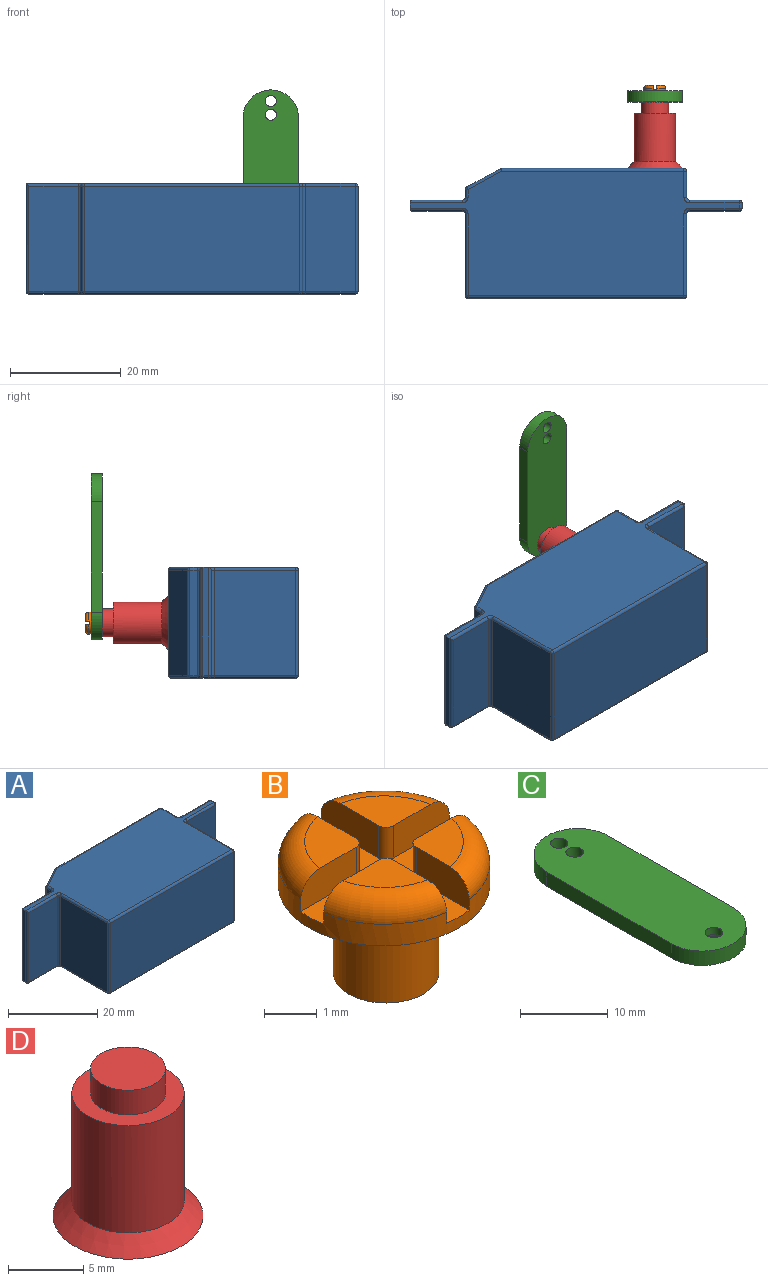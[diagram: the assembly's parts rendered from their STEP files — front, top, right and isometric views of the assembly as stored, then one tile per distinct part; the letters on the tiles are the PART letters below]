
ASSEMBLY  parts=4 mates=3
PART A: 77 faces, bbox 60x23.5x20 mm
  f0: plane 19x1.43mm, normal (-1,0,0), area 27.2mm2, adj f65,f70,f73,f76
  f1: plane 19x9mm, normal (0,1,0), area 171mm2, adj f64,f68,f72,f73
  f2: plane 19.5x1mm, normal (-1,0,0), area 19.5mm2, adj f13,f51,f59,f68
  f3: plane 19x9mm, normal (0,-1,0), area 171mm2, adj f42,f47,f51,f52
  f4: plane 19x14.77mm, normal (-1,0,0), area 280.6mm2, adj f32,f37,f42,f43
  f5: plane 39x19mm, normal (0,-1,0), area 741mm2, adj f22,f27,f32,f33
  f6: plane 19x14.77mm, normal (1,0,0), area 280.6mm2, adj f16,f17,f22,f23
  f7: plane 19x9mm, normal (0,-1,0), area 171mm2, adj f15,f16,f25,f26
  f8: plane 19x1mm, normal (1,0,0), area 19mm2, adj f24,f25,f35,f36
  f9: plane 19x9mm, normal (0,1,0), area 171mm2, adj f34,f35,f45,f46
  f10: plane 19x4.73mm, normal (1,0,0), area 89.9mm2, adj f44,f45,f54,f55
  f11: plane 32.89x19mm, normal (0,1,0), area 625mm2, adj f53,f54,f61,f62
  f12: plane 19x6.11mm, normal (-0.48,0.88,0), area 131.8mm2, adj f60,f61,f70,f71
  f13: plane 59.5x22.5mm, normal (0,0,1), area 888.8mm2, adj f2,f17,f20,f26,f27,f36,f37,f41
  f14: plane 59x22.5mm, normal (0,0,-1), area 888.3mm2, adj f15,f18,f23,f24,f33,f34,f39,f43
  f15: cylinder r=0.5mm len=9mm, axis (1,0,0), area 7.1mm2, adj f7,f14,f18,f19
  f16: cylinder r=0.5mm len=19mm, axis (0,0,-1), area 14.9mm2, adj f6,f7,f18,f20
  f17: cylinder r=0.5mm len=14.77mm, axis (0,-1,0), area 11.6mm2, adj f6,f13,f20,f21
  f18: torus R=1mm, axis (0,0,1), area 0.8mm2, adj f14,f15,f16,f23
  f19: sphere r=0.5mm, area 0.4mm2, adj f15,f24,f25
  f20: torus R=1mm, axis (0,0,1), area 0.8mm2, adj f13,f16,f17,f26
  f21: sphere r=0.5mm, area 0.4mm2, adj f17,f22,f27
  f22: cylinder r=0.5mm len=19mm, axis (0,0,1), area 14.9mm2, adj f5,f6,f21,f28
  f23: cylinder r=0.5mm len=14.77mm, axis (0,1,0), area 11.6mm2, adj f6,f14,f18,f28
  f24: cylinder r=0.5mm len=1mm, axis (0,1,0), area 0.8mm2, adj f8,f14,f19,f29
  f25: cylinder r=0.5mm len=19mm, axis (0,0,1), area 14.9mm2, adj f7,f8,f19,f30
  f26: cylinder r=0.5mm len=9mm, axis (-1,0,0), area 7.1mm2, adj f7,f13,f20,f30
  f27: cylinder r=0.5mm len=39mm, axis (-1,0,0), area 30.6mm2, adj f5,f13,f21,f31
  f28: sphere r=0.5mm, area 0.4mm2, adj f22,f23,f33
  f29: sphere r=0.5mm, area 0.4mm2, adj f24,f34,f35
  f30: sphere r=0.5mm, area 0.4mm2, adj f25,f26,f36
  f31: sphere r=0.5mm, area 0.4mm2, adj f27,f32,f37
  f32: cylinder r=0.5mm len=19mm, axis (0,0,-1), area 14.9mm2, adj f4,f5,f31,f38
  f33: cylinder r=0.5mm len=39mm, axis (1,0,0), area 30.6mm2, adj f5,f14,f28,f38
  f34: cylinder r=0.5mm len=9mm, axis (-1,0,0), area 7.1mm2, adj f9,f14,f29,f39
  f35: cylinder r=0.5mm len=19mm, axis (0,0,-1), area 14.9mm2, adj f8,f9,f29,f40
  f36: cylinder r=0.5mm len=1mm, axis (0,-1,0), area 0.8mm2, adj f8,f13,f30,f40
  f37: cylinder r=0.5mm len=14.77mm, axis (0,1,0), area 11.6mm2, adj f4,f13,f31,f41
  f38: sphere r=0.5mm, area 0.4mm2, adj f32,f33,f43
  f39: torus R=1mm, axis (0,0,1), area 0.8mm2, adj f14,f34,f44,f45
  f40: sphere r=0.5mm, area 0.4mm2, adj f35,f36,f46
  f41: torus R=1mm, axis (0,0,1), area 0.8mm2, adj f13,f37,f42,f47
  f42: cylinder r=0.5mm len=19mm, axis (0,0,-1), area 14.9mm2, adj f3,f4,f41,f48
  f43: cylinder r=0.5mm len=14.77mm, axis (0,-1,0), area 11.6mm2, adj f4,f14,f38,f48
  f44: cylinder r=0.5mm len=4.73mm, axis (0,1,0), area 3.7mm2, adj f10,f14,f39,f49
  f45: cylinder r=0.5mm len=19mm, axis (0,0,1), area 14.9mm2, adj f9,f10,f39,f50
  f46: cylinder r=0.5mm len=9mm, axis (1,0,0), area 7.1mm2, adj f9,f13,f40,f50
  f47: cylinder r=0.5mm len=9.5mm, axis (-1,0,0), area 7.3mm2, adj f3,f13,f41,f51
  f48: torus R=1mm, axis (0,0,1), area 0.8mm2, adj f14,f42,f43,f52
  f49: sphere r=0.5mm, area 0.4mm2, adj f44,f53,f54
  f50: torus R=1mm, axis (0,0,1), area 0.8mm2, adj f13,f45,f46,f55
  f51: cylinder r=0.5mm len=19.5mm, axis (0,0,1), area 15.2mm2, adj f2,f3,f47,f56
  f52: cylinder r=0.5mm len=9mm, axis (1,0,0), area 7.1mm2, adj f3,f14,f48,f56
  f53: cylinder r=0.5mm len=32.89mm, axis (-1,0,0), area 25.8mm2, adj f11,f14,f49,f57
  f54: cylinder r=0.5mm len=19mm, axis (0,0,1), area 14.9mm2, adj f10,f11,f49,f58
  f55: cylinder r=0.5mm len=4.73mm, axis (0,-1,0), area 3.7mm2, adj f10,f13,f50,f58
  f56: sphere r=0.5mm, area 0.4mm2, adj f51,f52,f59
  f57: sphere r=0.5mm, area 0.1mm2, adj f53,f60,f61
  f58: sphere r=0.5mm, area 0.4mm2, adj f54,f55,f62
  f59: cylinder r=0.5mm len=1mm, axis (0,-1,0), area 0.8mm2, adj f2,f14,f56,f63
  f60: cylinder r=0.5mm len=6.34mm, axis (-0.88,-0.48,0), area 5.5mm2, adj f12,f14,f57,f66
  f61: cylinder r=0.5mm len=19mm, axis (0,0,1), area 4.7mm2, adj f11,f12,f57,f67
  f62: cylinder r=0.5mm len=32.89mm, axis (1,0,0), area 25.8mm2, adj f11,f13,f58,f67
  f63: sphere r=0.5mm, area 0.4mm2, adj f59,f64,f68
  f64: cylinder r=0.5mm len=9mm, axis (-1,0,0), area 7.1mm2, adj f1,f14,f63,f69
  f65: cylinder r=0.5mm len=1.43mm, axis (0,-1,0), area 1.1mm2, adj f0,f14,f66,f69
  f66: sphere r=0.5mm, area 0.3mm2, adj f60,f65,f70
  f67: sphere r=0.5mm, area 0.1mm2, adj f61,f62,f71
  f68: cylinder r=0.5mm len=19.5mm, axis (0,0,-1), area 15.2mm2, adj f1,f2,f63,f72
  f69: torus R=1mm, axis (0,0,1), area 0.8mm2, adj f14,f64,f65,f73
  f70: cylinder r=0.5mm len=19mm, axis (0,0,1), area 10.2mm2, adj f0,f12,f66,f74
  f71: cylinder r=0.5mm len=6.34mm, axis (0.88,0.48,0), area 5.5mm2, adj f12,f13,f67,f74
  f72: cylinder r=0.5mm len=9.5mm, axis (1,0,0), area 7.3mm2, adj f1,f13,f68,f75
  f73: cylinder r=0.5mm len=19mm, axis (0,0,1), area 14.9mm2, adj f0,f1,f69,f75
  f74: sphere r=0.5mm, area 0.3mm2, adj f70,f71,f76
  f75: torus R=1mm, axis (0,0,1), area 0.8mm2, adj f13,f72,f73,f76
  f76: cylinder r=0.5mm len=1.43mm, axis (0,1,0), area 1.1mm2, adj f0,f13,f74,f75
PART B: 25 faces, bbox 4.3x4.3x3 mm
  f0: cylinder r=1mm len=2mm, axis (0,0,1), area 12.6mm2, adj f1,f2
  f1: plane 2x2mm, normal (0,0,-1), area 3.1mm2, adj f0
  f2: plane 4x4mm, normal (0,0,-1), area 9.4mm2, adj f0,f3
  f3: cylinder r=2mm len=4mm, axis (0,0,-1), area 5.7mm2, adj f2,f4,f5,f7,f8,f10,f11,f13
  f4: plane 1.54x0.75mm, normal (-1,0,0), area 1.1mm2, adj f3,f6,f16,f19,f23
  f5: plane 1.49x0.75mm, normal (0,-1,0), area 1.1mm2, adj f3,f6,f16,f19,f23
  f6: plane 1.23x1.18mm, normal (0,0,1), area 1mm2, adj f4,f5,f19,f23
  f7: plane 1.49x0.75mm, normal (0,-1,0), area 1.1mm2, adj f3,f9,f16,f20,f24
  f8: plane 1.54x0.75mm, normal (1,0,0), area 1.1mm2, adj f3,f9,f16,f20,f24
  f9: plane 1.23x1.18mm, normal (0,0,1), area 1mm2, adj f7,f8,f20,f24
  f10: plane 1.42x0.75mm, normal (1,0,0), area 1mm2, adj f3,f12,f16,f17,f21
  f11: plane 1.47x0.75mm, normal (0,1,0), area 1mm2, adj f3,f12,f16,f17,f21
  f12: plane 1.16x1.11mm, normal (0,0,1), area 0.9mm2, adj f10,f11,f17,f21
  f13: plane 1.47x0.75mm, normal (0,1,0), area 1mm2, adj f3,f15,f16,f18,f22
  f14: plane 1.42x0.75mm, normal (-1,0,0), area 1mm2, adj f3,f15,f16,f18,f22
  f15: plane 1.16x1.11mm, normal (0,0,1), area 0.9mm2, adj f13,f14,f18,f22
  f16: plane 4x4mm, normal (0,0,1), area 4.5mm2, adj f3,f4,f5,f7,f8,f10,f11,f13
  f17: cylinder r=0.2mm len=0.75mm, axis (0,0,-1), area 0.2mm2, adj f10,f11,f12,f16
  f18: cylinder r=0.2mm len=0.75mm, axis (0,0,1), area 0.2mm2, adj f13,f14,f15,f16
  f19: cylinder r=0.2mm len=0.75mm, axis (0,0,-1), area 0.2mm2, adj f4,f5,f6,f16
  f20: cylinder r=0.2mm len=0.75mm, axis (0,0,1), area 0.2mm2, adj f7,f8,f9,f16
  f21: torus R=1.5mm, axis (0,0,1), area 1.7mm2, adj f3,f10,f11,f12
  f22: torus R=1.5mm, axis (0,0,1), area 1.7mm2, adj f3,f13,f14,f15
  f23: torus R=1.5mm, axis (0,0,1), area 1.8mm2, adj f3,f4,f5,f6
  f24: torus R=1.5mm, axis (0,0,1), area 1.8mm2, adj f3,f7,f8,f9
PART C: 11 faces, bbox 10x30x2 mm
  f0: plane 20x2mm, normal (-1,0,0), area 40mm2, adj f2,f3,f9,f10
  f1: plane 20x2mm, normal (1,0,0), area 40mm2, adj f2,f3,f9,f10
  f2: plane 30x10mm, normal (0,0,1), area 269.1mm2, adj f0,f1,f4,f5,f6,f9,f10
  f3: plane 30x10mm, normal (0,0,-1), area 259.7mm2, adj f0,f1,f4,f5,f8,f9,f10
  f4: cylinder r=1mm len=2mm, axis (0,0,-1), area 12.6mm2, adj f2,f3
  f5: cylinder r=1mm len=2mm, axis (0,0,-1), area 12.6mm2, adj f2,f3
  f6: cylinder r=1mm len=2mm, axis (0,0,-1), area 6.3mm2, adj f2,f7
  f7: plane 4x4mm, normal (0,0,-1), area 9.4mm2, adj f6,f8
  f8: cylinder r=2mm len=4mm, axis (0,0,-1), area 12.6mm2, adj f3,f7
  f9: cylinder r=5mm len=10mm, axis (0,0,-1), area 31.4mm2, adj f0,f1,f2,f3
  f10: cylinder r=5mm len=10mm, axis (0,0,1), area 31.4mm2, adj f0,f1,f2,f3
PART D: 6 faces, bbox 10x10x12 mm
  f0: plane 10x10mm, normal (0,0,-1), area 78.5mm2, adj f5
  f1: cylinder r=3.75mm len=8.75mm, axis (0,0,-1), area 206.2mm2, adj f2,f5
  f2: plane 7.5x7.5mm, normal (0,0,1), area 24.5mm2, adj f1,f4
  f3: plane 5x5mm, normal (0,0,1), area 19.6mm2, adj f4
  f4: cylinder r=2.5mm len=5mm, axis (0,0,-1), area 31.4mm2, adj f2,f3
  f5: cone r=3mm half-angle=45deg, axis (0,0,-1), area 48.6mm2, adj f0,f1
PLACE A t=(-9.81,-8.5,-1.79)mm
PLACE B rot(axis=(-1,0,0),90deg) t=(-28.07,11.23,8.21)mm
PLACE C rot(axis=(1,0,0),90deg) t=(13.07,11.23,-13.77)mm
PLACE D rot(axis=(0,0.71,0.71),180deg) t=(-28.07,-2.77,8.21)mm
MATE cylindrical C.f6 <-> D.f4  axis (0,-1,0) through (-28.07,9.23,8.21)mm
MATE planar D.f5 <-> A.f11  axis (0,-1,0) through (-28.07,-2.77,8.21)mm
MATE cylindrical B.f0 <-> C.f6  axis (0,-1,0) through (-28.07,9.23,8.21)mm
